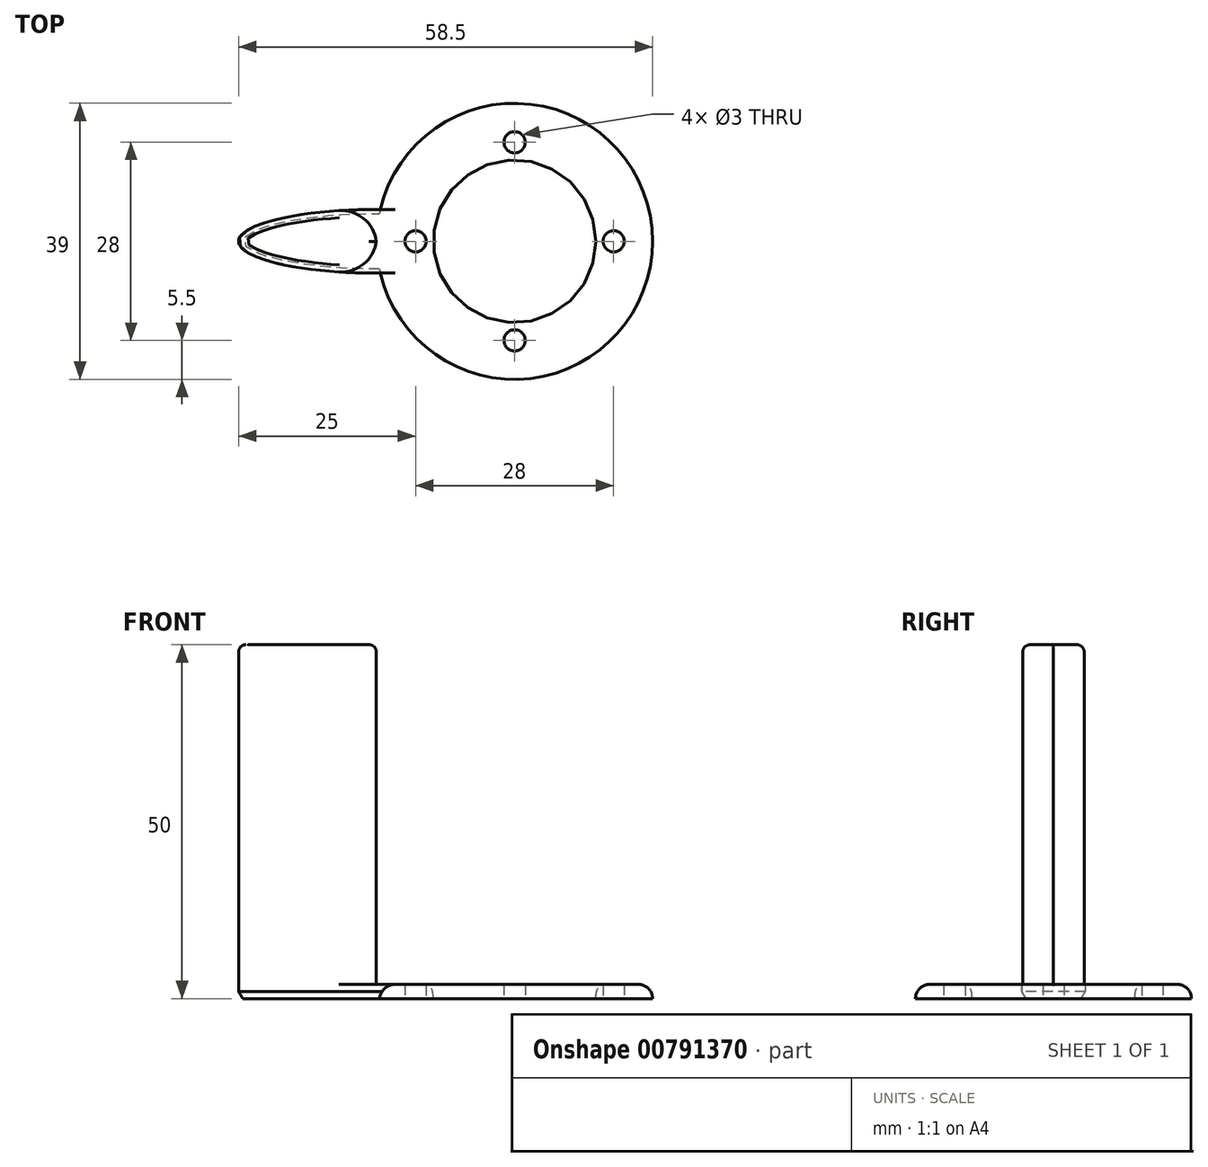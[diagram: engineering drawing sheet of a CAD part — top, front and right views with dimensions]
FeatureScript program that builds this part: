
annotation { "Feature Type Name" : "Feature", "Feature Type Description" : "" }
export const myFeature = defineFeature(function(context is Context, id is Id, definition is map)
    precondition{}
    {
        {
            var Q0;
            Q0=qCreatedBy(makeId("Top.planeOp"),FACE);
            var sketch = newSketch(context, id + "F0", { "sketchPlane" : qUnion([Q0])});
            skCircle(sketch, "E0", {"center": v(0, 0) * mm, "radius": 11.5 * mm});
            skCircle(sketch, "E1", {"center": v(0, 0) * mm, "radius": 19.5 * mm});
            skEllipse(sketch, "E2", {"center": v(-19.5, 0) * mm, "majorRadius": 19.5 * mm, "minorRadius": 4.5 * mm, "majorAxis": v(1, 0)});
            skCircle(sketch, "E3", {"center": v(-14, 0) * mm, "radius": 1.5 * mm});
            skCircle(sketch, "E4.1.0", {"center": v(0, -14) * mm, "radius": 1.5 * mm});
            skCircle(sketch, "E4.2.0", {"center": v(14, 0) * mm, "radius": 1.5 * mm});
            skCircle(sketch, "E4.3.0", {"center": v(0, 14) * mm, "radius": 1.5 * mm});
            skSolve(sketch);
        }
        {
            var Q0;
            Q0=makeQuery(id+"F0.imprint","IMPRINT",FACE,{"disambiguationData":[TD([[makeQuery(id+"F0.imprint","IMPRINT",EDGE,{"derivedFrom":sQuery(id+"F0.wireOp",EDGE,"E4.1.0")}),-1.0]])]});
            var Q1;
            Q1=makeQuery(id+"F0.imprint","IMPRINT",FACE,{"disambiguationData":[TD([[makeQuery(id+"F0.imprint","IMPRINT",EDGE,{"derivedFrom":sQuery(id+"F0.wireOp",EDGE,"E3")}),-1.0]])]});
            extrude(context, id + "F1", {"entities" : qUnion([Q0, Q1]), "depth" : 2 * mm, "offsetDistance" : 25 * mm});
        }
        {
            var Q0;
            {var subQ0=sQuery(id+"F0.wireOp",EDGE,"E2");var subQ1=sQuery(id+"F0.wireOp",EDGE,"E1");var subQ2=makeQuery(id+"F0.imprint","INTERSECT",VERTEX,{"disambiguationData":[OD(0.0)],"derivedFrom":[subQ1,subQ0]});Q0=makeQuery(id+"F0.imprint","IMPRINT",FACE,{"disambiguationData":[TD([[makeQuery(id+"F0.imprint","IMPRINT",EDGE,{"disambiguationData":[TD([[subQ2,-1.0]])],"derivedFrom":subQ1}),-1.0]])]});}
            extrude(context, id + "F2", {"entities" : qUnion([Q0]), "operationType" : NewBodyOperationType.ADD, "depth" : 50 * mm, "offsetDistance" : 25 * mm});
        }
        {
            var Q0;
            {var subQ0=sQuery(id+"F0.wireOp",EDGE,"E1");Q0=makeQuery(id+"F2.boolean.opBoolean","SPLIT",EDGE,{"disambiguationData":[topologyDisambiguationEdgeConnected([makeQuery(id+"F2.opExtrude","SWEPT_FACE",FACE,{"disambiguationData":[OSD([subQ0])]})])],"derivedFrom":makeQuery(id+"F1.opExtrude","CAP_EDGE",EDGE,{"disambiguationData":[OSD([subQ0])],"isStart":false})});}
            fillet(context, id + "F3", {"entities" : qUnion([Q0]), "radius" : 2 * mm, "tangentPropagation" : true, "allowEdgeOverflow" : false});
        }
        {
            var Q0;
            {var subQ0=sQuery(id+"F0.wireOp",EDGE,"E1");var subQ1=sQuery(id+"F0.wireOp",EDGE,"E2");Q0=makeQuery(id+"F2.boolean.opBoolean","SPLIT",EDGE,{"disambiguationData":[topologyDisambiguationEdgeConnected([makeQuery(id+"F1.opExtrude","SWEPT_FACE",FACE,{"disambiguationData":[OSD([subQ0])]})])],"derivedFrom":makeQuery(id+"F2.opExtrude","SWEPT_EDGE",EDGE,{"disambiguationData":[OSD([subQ0,subQ1]),TDD([makeQuery(id+"F0.imprint","INTERSECT",VERTEX,{"disambiguationData":[OD(1.0)],"derivedFrom":[subQ0,subQ1]})])]})});}
            var Q1;
            {var subQ0=sQuery(id+"F0.wireOp",EDGE,"E1");var subQ1=sQuery(id+"F0.wireOp",EDGE,"E2");Q1=makeQuery(id+"F2.boolean.opBoolean","SPLIT",EDGE,{"disambiguationData":[topologyDisambiguationEdgeConnected([makeQuery(id+"F1.opExtrude","SWEPT_FACE",FACE,{"disambiguationData":[OSD([subQ0])]})])],"derivedFrom":makeQuery(id+"F2.opExtrude","SWEPT_EDGE",EDGE,{"disambiguationData":[OSD([subQ0,subQ1]),TDD([makeQuery(id+"F0.imprint","INTERSECT",VERTEX,{"disambiguationData":[OD(0.0)],"derivedFrom":[subQ0,subQ1]})])]})});}
            fillet(context, id + "F4", {"entities" : qUnion([Q0, Q1]), "radius" : 5 * mm, "tangentPropagation" : true, "allowEdgeOverflow" : false});
        }
        {
            var Q0;
            Q0=makeQuery(id+"F2.opExtrude","CAP_FACE",FACE,{"disambiguationData":[OSD([sQuery(id+"F0.wireOp",EDGE,"E1"),sQuery(id+"F0.wireOp",EDGE,"E2")])],"isStart":false});
            fillet(context, id + "F5", {"entities" : qUnion([Q0]), "radius" : 1 * mm, "tangentPropagation" : true, "allowEdgeOverflow" : false});
        }
        {
            var Q0;
            Q0=makeQuery(id+"F2.opExtrude","CAP_EDGE",EDGE,{"disambiguationData":[OSD([sQuery(id+"F0.wireOp",EDGE,"E2")])],"isStart":true});
            var Q1;
            Q1=makeQuery(id+"F1.opExtrude","CAP_EDGE",EDGE,{"disambiguationData":[OSD([sQuery(id+"F0.wireOp",EDGE,"E1")])],"isStart":true});
            var Q2;
            {var subQ0=sQuery(id+"F0.wireOp",EDGE,"E2");var subQ1=sQuery(id+"F0.wireOp",EDGE,"E1");Q2=makeQuery(id+"F4.opFillet","BLEND_EDGE",EDGE,{"blendedFrom":[makeQuery(id+"F2.boolean.opBoolean","SPLIT",EDGE,{"disambiguationData":[topologyDisambiguationEdgeConnected([makeQuery(id+"F1.opExtrude","SWEPT_FACE",FACE,{"disambiguationData":[OSD([subQ1])]})])],"derivedFrom":makeQuery(id+"F2.opExtrude","SWEPT_EDGE",EDGE,{"disambiguationData":[OSD([subQ1,subQ0]),TDD([makeQuery(id+"F0.imprint","INTERSECT",VERTEX,{"disambiguationData":[OD(1.0)],"derivedFrom":[subQ1,subQ0]})])]})}),makeQuery(id+"F2.boolean.opBoolean","MERGE",FACE,{"derivedFrom":[makeQuery(id+"F1.opExtrude","CAP_FACE",FACE,{"disambiguationData":[OSD([sQuery(id+"F0.wireOp",EDGE,"E0"),subQ1,sQuery(id+"F0.wireOp",EDGE,"E3"),sQuery(id+"F0.wireOp",EDGE,"E4.1.0"),sQuery(id+"F0.wireOp",EDGE,"E4.2.0"),sQuery(id+"F0.wireOp",EDGE,"E4.3.0")])],"isStart":true}),makeQuery(id+"F2.opExtrude","CAP_FACE",FACE,{"disambiguationData":[OSD([subQ1,subQ0])],"isStart":true})]})],"blendedInto":[makeQuery(id+"F2.boolean.opBoolean","MERGE",FACE,{"derivedFrom":[makeQuery(id+"F1.opExtrude","CAP_FACE",FACE,{"disambiguationData":[OSD([sQuery(id+"F0.wireOp",EDGE,"E0"),subQ1,sQuery(id+"F0.wireOp",EDGE,"E3"),sQuery(id+"F0.wireOp",EDGE,"E4.1.0"),sQuery(id+"F0.wireOp",EDGE,"E4.2.0"),sQuery(id+"F0.wireOp",EDGE,"E4.3.0")])],"isStart":true}),makeQuery(id+"F2.opExtrude","CAP_FACE",FACE,{"disambiguationData":[OSD([subQ1,subQ0])],"isStart":true})]})]});}
            var Q3;
            {var subQ0=sQuery(id+"F0.wireOp",EDGE,"E2");var subQ1=sQuery(id+"F0.wireOp",EDGE,"E1");Q3=makeQuery(id+"F4.opFillet","BLEND_EDGE",EDGE,{"blendedFrom":[makeQuery(id+"F2.boolean.opBoolean","SPLIT",EDGE,{"disambiguationData":[topologyDisambiguationEdgeConnected([makeQuery(id+"F1.opExtrude","SWEPT_FACE",FACE,{"disambiguationData":[OSD([subQ1])]})])],"derivedFrom":makeQuery(id+"F2.opExtrude","SWEPT_EDGE",EDGE,{"disambiguationData":[OSD([subQ1,subQ0]),TDD([makeQuery(id+"F0.imprint","INTERSECT",VERTEX,{"disambiguationData":[OD(0.0)],"derivedFrom":[subQ1,subQ0]})])]})}),makeQuery(id+"F2.boolean.opBoolean","MERGE",FACE,{"derivedFrom":[makeQuery(id+"F1.opExtrude","CAP_FACE",FACE,{"disambiguationData":[OSD([sQuery(id+"F0.wireOp",EDGE,"E0"),subQ1,sQuery(id+"F0.wireOp",EDGE,"E3"),sQuery(id+"F0.wireOp",EDGE,"E4.1.0"),sQuery(id+"F0.wireOp",EDGE,"E4.2.0"),sQuery(id+"F0.wireOp",EDGE,"E4.3.0")])],"isStart":true}),makeQuery(id+"F2.opExtrude","CAP_FACE",FACE,{"disambiguationData":[OSD([subQ1,subQ0])],"isStart":true})]})],"blendedInto":[makeQuery(id+"F2.boolean.opBoolean","MERGE",FACE,{"derivedFrom":[makeQuery(id+"F1.opExtrude","CAP_FACE",FACE,{"disambiguationData":[OSD([sQuery(id+"F0.wireOp",EDGE,"E0"),subQ1,sQuery(id+"F0.wireOp",EDGE,"E3"),sQuery(id+"F0.wireOp",EDGE,"E4.1.0"),sQuery(id+"F0.wireOp",EDGE,"E4.2.0"),sQuery(id+"F0.wireOp",EDGE,"E4.3.0")])],"isStart":true}),makeQuery(id+"F2.opExtrude","CAP_FACE",FACE,{"disambiguationData":[OSD([subQ1,subQ0])],"isStart":true})]})]});}
            chamfer(context, id + "F6", {"entities" : qUnion([Q0, Q1, Q2, Q3]), "chamferType" : ChamferType.OFFSET_ANGLE, "width" : 1 * mm, "oppositeDirection" : false, "angle" : 30 * degree, "tangentPropagation" : true});
        }
        {
            var Q0;
            Q0=makeQuery(id+"F1.opExtrude","CAP_EDGE",EDGE,{"disambiguationData":[OSD([sQuery(id+"F0.wireOp",EDGE,"E0")])],"isStart":false});
            fillet(context, id + "F7", {"entities" : qUnion([Q0]), "radius" : 2 * mm, "tangentPropagation" : true, "rho" : 0.6, "crossSection" : FilletCrossSection.CONIC, "allowEdgeOverflow" : false});
        }
    });
